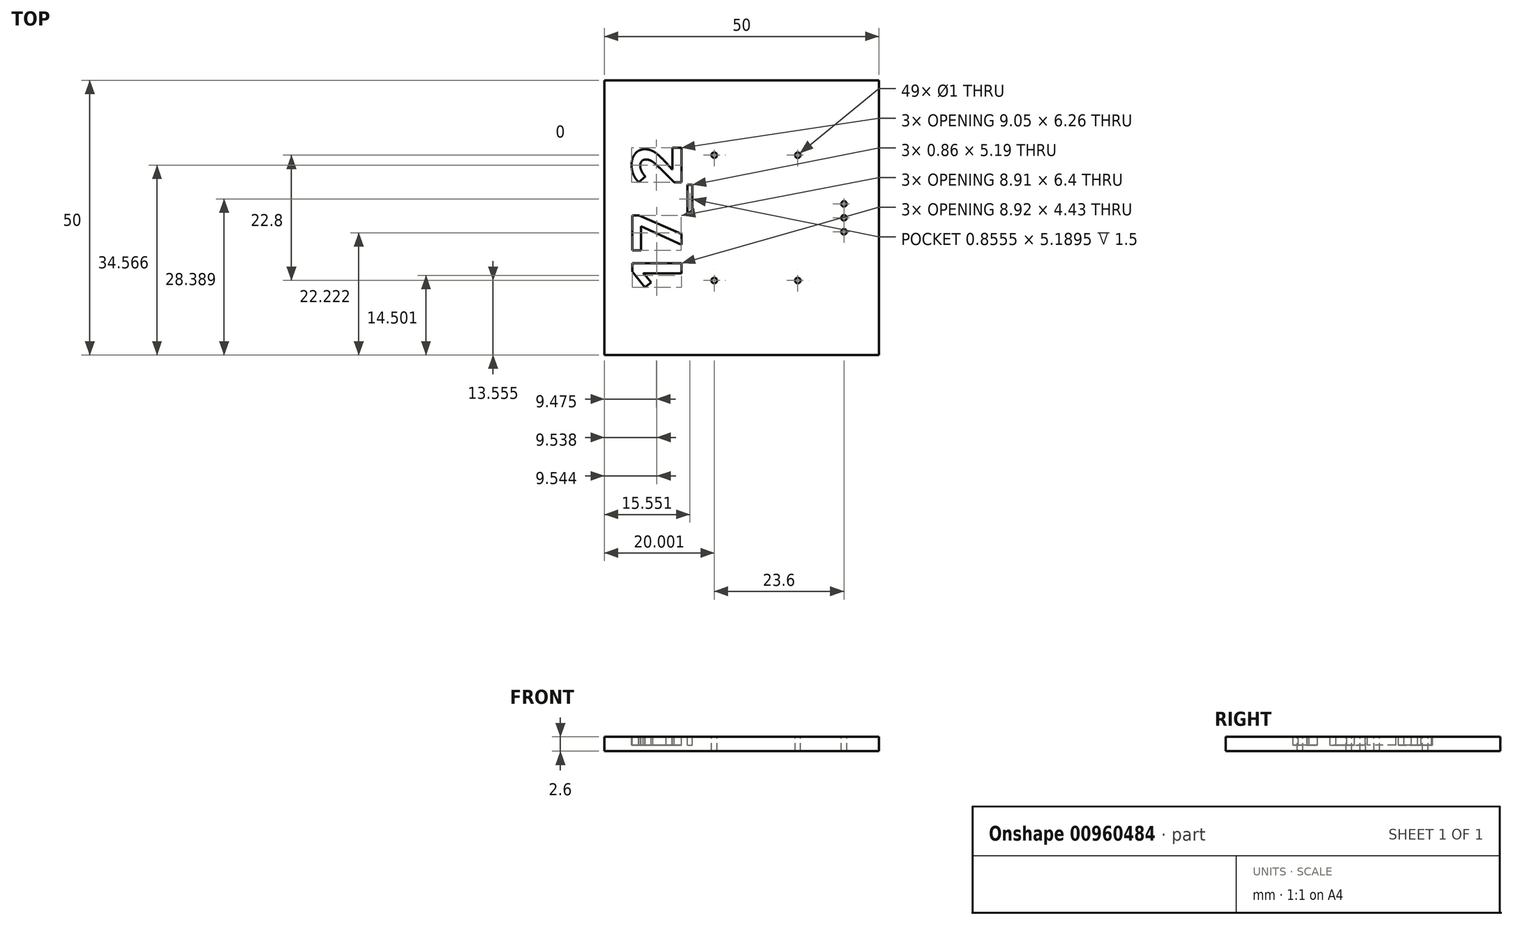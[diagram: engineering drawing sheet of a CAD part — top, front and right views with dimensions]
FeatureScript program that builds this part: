
annotation { "Feature Type Name" : "Feature", "Feature Type Description" : "" }
export const myFeature = defineFeature(function(context is Context, id is Id, definition is map)
    precondition{}
    {
        {
            var Q0;
            Q0=qCreatedBy(makeId("Top.planeOp"),FACE);
            var sketch = newSketch(context, id + "F0", { "sketchPlane" : qUnion([Q0])});
            skLineSegment(sketch, "E0.bottom", {"start": v(-43.16, 28.34) * mm, "end": v(6.84, 28.34) * mm});
            skLineSegment(sketch, "E0.top", {"start": v(-43.16, -21.66) * mm, "end": v(6.84, -21.66) * mm});
            skLineSegment(sketch, "E0.left", {"start": v(-43.16, 28.34) * mm, "end": v(-43.16, -21.66) * mm});
            skLineSegment(sketch, "E0.right", {"start": v(6.84, 28.34) * mm, "end": v(6.84, -21.66) * mm});
            skSolve(sketch);
        }
        {
            var Q0;
            Q0=makeQuery(id+"F0.imprint","IMPRINT",FACE,{"disambiguationData":[TD([[makeQuery(id+"F0.imprint","IMPRINT",EDGE,{"derivedFrom":sQuery(id+"F0.wireOp",EDGE,"E0.bottom")}),-1.0]])]});
            extrude(context, id + "F1", {"entities" : qUnion([Q0]), "depth" : 2.6 * mm, "offsetDistance" : 25 * mm});
        }
        {
            var Q0;
            Q0=makeQuery(id+"F1.opExtrude","CAP_FACE",FACE,{"disambiguationData":[OSD([sQuery(id+"F0.wireOp",EDGE,"E0.bottom"),sQuery(id+"F0.wireOp",EDGE,"E0.top"),sQuery(id+"F0.wireOp",EDGE,"E0.left"),sQuery(id+"F0.wireOp",EDGE,"E0.right")])],"isStart":false});
            var sketch = newSketch(context, id + "F2", { "sketchPlane" : qUnion([Q0])});
            skText(sketch, "E1", { "text": "17_2", "fontName": "OpenSans-Bold.ttf"});
            const initialGuessF2  = {"E1": [-0.02916, -0.01011, 0, 1, 0.009]};
            skSetInitialGuess(sketch, initialGuessF2);
            skSolve(sketch);
        }
        {
            var Q0;
            Q0=qSketchRegion(id+"F2",true);
            extrude(context, id + "F3", {"entities" : qUnion([Q0]), "operationType" : NewBodyOperationType.REMOVE, "oppositeDirection" : true, "depth" : 1.5 * mm, "offsetDistance" : 25 * mm});
        }
        {
            var Q0;
            {var subQ0=sQuery(id+"F0.wireOp",EDGE,"E0.left");var subQ1=sQuery(id+"F0.wireOp",EDGE,"E0.bottom");var subQ2=sQuery(id+"F0.wireOp",EDGE,"E0.right");var subQ3=sQuery(id+"F0.wireOp",EDGE,"E0.top");Q0=makeQuery(id+"F3.boolean.opBoolean","SPLIT",FACE,{"disambiguationData":[TD([makeQuery(id+"F1.opExtrude","SWEPT_FACE",FACE,{"disambiguationData":[OSD([subQ1])]})])],"derivedFrom":makeQuery(id+"F1.opExtrude","CAP_FACE",FACE,{"disambiguationData":[OSD([subQ1,subQ3,subQ0,subQ2])],"isStart":false})});}
            var sketch = newSketch(context, id + "F4", { "sketchPlane" : qUnion([Q0])});
            skCircle(sketch, "E2", {"center": v(-23.16, -8.1) * mm, "radius": 0.5 * mm});
            skCircle(sketch, "E3", {"center": v(-23.16, 14.7) * mm, "radius": 0.5 * mm});
            skCircle(sketch, "E4", {"center": v(-7.96, -8.1) * mm, "radius": 0.5 * mm});
            skCircle(sketch, "E5", {"center": v(-7.96, 14.7) * mm, "radius": 0.5 * mm});
            skCircle(sketch, "E6", {"center": v(0.44, 0.76) * mm, "radius": 0.5 * mm});
            skCircle(sketch, "E7", {"center": v(0.44, 3.3) * mm, "radius": 0.5 * mm});
            skCircle(sketch, "E8", {"center": v(0.44, 5.84) * mm, "radius": 0.5 * mm});
            skSolve(sketch);
        }
        {
            var Q0;
            Q0 = qSketchRegion(id + "F4", true);
            extrude(context, id + "F5", {"entities" : qUnion([Q0]), "operationType" : NewBodyOperationType.REMOVE, "endBound" : BoundingType.UP_TO_NEXT, "oppositeDirection" : true, "depth" : 25 * mm, "offsetDistance" : 25 * mm});
        }
    });
